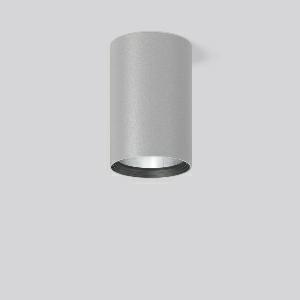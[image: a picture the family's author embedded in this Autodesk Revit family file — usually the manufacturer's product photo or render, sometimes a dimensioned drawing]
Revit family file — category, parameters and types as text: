
# Revit family: heledon_maxi_a_931226_004_76_c983
name_source: partatom
category: Lighting Fixtures
units: mm (PartAtom-declared; Revit-internal decimal feet)

## family parameters
Cut with Voids When Loaded = No
Host = Face
Light Source = No
Part Type = Normal
Room Calculation Point = No
Round Connector Dimension = Use Diameter
Shared = No

## types (1)
- HELEDON maxi A (1 x LED Modul 930, 4150 lm, 3000)
    Apparent Load = 35 VA
    Approval mark = CE
    CIE Flux Codes = 97 100 100 100 100
    Color Rendering = 90
    Color Temperature = 3000
    Default Elevation = 1800 mm
    Description = Series: HELEDON maxi
Cylindrical surface-mounted downlight. Housing: die-cast aluminium, powder-coated. Internal ceiling frame polycarbonate with bayonet mounting. Black plastic ring and recessed LED to prevent glare from the side. Optical assembly with reflector made of MIRO-Silver with 98% total light reflection for outstanding efficiency - can be changed without tools. Best colour rendering index Ra>90. Suitable for Ceiling mounting. Easy installation with a separate ceiling frame with bayonet mounting and plug connection. Driver integrated. Connected via plug-in connector. High quality converter without flickering and stroboscopic effect. The following accessories can be mounted without use of tools: interchangeable lenses, decorative glasses, honeycomb louvre, clear and frosted diffusers, white interchangeable plastic ring. 
Colour: silver
Diameter: 123 mm
Height: 183 mm
Lamp: LED
Socket: without socket
Colour temperature: 3000K
Colour rendering index (CRI): 92
System power: 35 W
Rated luminous flux: 4150 lm
Luminous efficiency: 119 lm/W
Control gear: Converter, dimmable, DALI
Protection class: I
Type of protection: IP 20
    Height = 183 mm
    Lamp = 1 x LED Modul 930
    Lamp Light Flux = 4150 lm
    Lamp count = 1
    Length = 123 mm
    Lifetime = 50000 h
    Luminous efficacy = 119 lm/W
    Manufacturer = RZB
    ModVariant = No
    Model = 931226.004.76
    Mounting Place = Ceiling
    Mounting Type = Surface mounted
    Number of Poles = 1
    OnlyDefault = Yes
    Power Factor = 1
    Product Name = HELEDON maxi A
    Product group = Surface mounted downlights
    ProductGroupID = 302
    Protection Class = Protection class I
    Protection Degree = IP 20
    RLX_Detail_Level = 1
    RLX_Emergency_Light_Flux = 0 lm
    RLX_Emergency_Type = 0
    RLX_Emergency_Type_DB = No
    RlxData = <blob elided: 98785 chars, md5=888a5d34>
    Socket = socket
    Standby Power = 0 W
    System Light Flux = 4150 lm
    System Power = 35 W
    Type Comments = Product without accessories
    Type Image = 931192.004.jpg
    URL = http://relux.com
    VarID = ---
    Voltage = 230 V
    Voltage Range = 220-240 V
    Weight = 0.00 kg
    Width = 0 mm  [stored 0 ft]

note: [stored X ft] marks values corroborated as IEEE doubles in the binary element streams (Revit-internal decimal feet)

## geometry (parser evidence)
native form markers: Blend x4, Sweep x9
no freeform markers — native parametric forms only
